# Revit family: Oval kiinteä korkeussäädettävä
name_source: partatom
category: Specialty Equipment
revit_build: Autodesk Revit 2015 (Build: 20160512_0715(x64)
units: mm (PartAtom-declared; Revit-internal decimal feet)

## types (4) — shared parameters
Assembly Code = 1336
Frame Colour = RAL 9016 - White
Height = 540 mm
Keynote = 523
Manufacturer = Väinö Korpinen Oy
Model = Oval
Support Height = 800 mm  [stored 2.62467 ft]
Thickness = 30 mm  [stored 0.0984252 ft]
URL = https://korpinen.com
Width = 106 mm

## per-type parameters (varying)
| type | 750 | 850 | Colour | Depth | Model ID |
| 20112R punainen | Yes | No | Elastomer - Red | 850 mm  [stored 2.78871 ft] | 20116R |
| 20116G harmaa | No | Yes | Elastomer - Grey | 850 mm  [stored 2.78871 ft] | 20116G |
| 20112G harmaa | Yes | No | Elastomer - Grey | 750 mm  [stored 2.46063 ft] | 20112G |
| 20116R punainen | No | Yes | Elastomer - Red | 850 mm  [stored 2.78871 ft] | 20116R |

note: [stored X ft] marks values corroborated as IEEE doubles in the binary element streams (Revit-internal decimal feet)

## geometry (parser evidence)
native form markers: Blend x6, Sweep x11
no freeform markers — native parametric forms only
